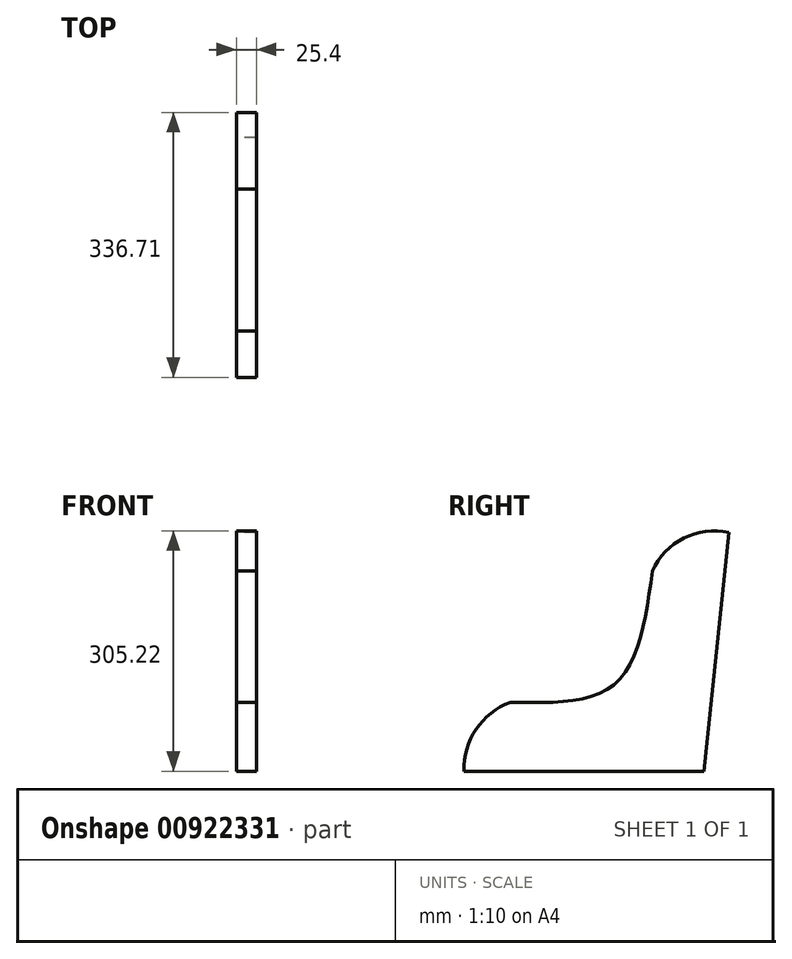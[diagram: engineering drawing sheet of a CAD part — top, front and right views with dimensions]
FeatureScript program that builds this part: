
annotation { "Feature Type Name" : "Feature", "Feature Type Description" : "" }
export const myFeature = defineFeature(function(context is Context, id is Id, definition is map)
    precondition{}
    {
        {
            var Q0;
            Q0=qCreatedBy(makeId("Right.planeOp"),FACE);
            var sketch = newSketch(context, id + "F0", { "sketchPlane" : qUnion([Q0])});
            skLineSegment(sketch, "E0", {"start": v(0, 0) * mm, "end": v(-304.8, 0) * mm});
            skLineSegment(sketch, "E1", {"start": v(0, 0) * mm, "end": v(31.86, 303.13) * mm});
            skArc(sketch, "E2", {"start": v(-246.15, 87.64) * mm, "mid": v(-289.58, 53.26) * mm, "end": v(-304.8, 0) * mm});
            skArc(sketch, "E3", {"start": v(31.86, 303.13) * mm, "mid": v(-25.67, 296.04) * mm, "end": v(-65.67, 254.1) * mm});
            skFitSpline(sketch, "E4", {"points": [v(-246.15, 87.64) * mm, v(-112.86, 111.24) * mm, v(-65.67, 254.1) * mm], "startDerivative": vector(318.06, -7.48) * mm, "endDerivative": vector(45.3, 337.34) * mm});
            skSolve(sketch);
        }
        {
            var Q0;
            Q0 = qSketchRegion(id + "F0", true);
            extrude(context, id + "F1", {"entities" : qUnion([Q0]), "depth" : 25.4 * mm, "offsetDistance" : 25.4 * mm});
        }
    });
